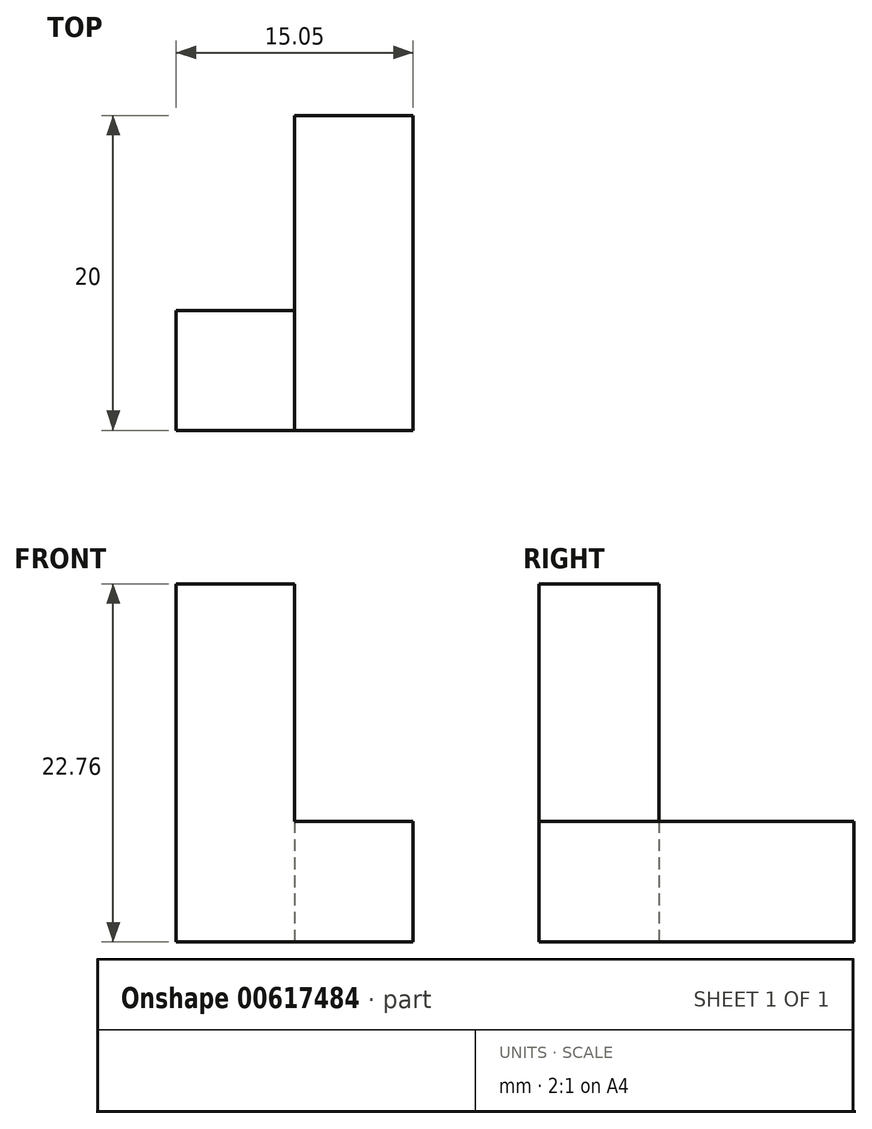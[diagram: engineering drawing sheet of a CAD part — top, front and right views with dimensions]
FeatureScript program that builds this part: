
annotation { "Feature Type Name" : "Feature", "Feature Type Description" : "" }
export const myFeature = defineFeature(function(context is Context, id is Id, definition is map)
    precondition{}
    {
        {
            var Q0;
            Q0=qCreatedBy(makeId("Front.planeOp"),FACE);
            var sketch = newSketch(context, id + "F0", { "sketchPlane" : qUnion([Q0])});
            skLineSegment(sketch, "E0", {"start": v(0, 0) * mm, "end": v(-15.05, 0) * mm});
            skLineSegment(sketch, "E1", {"start": v(-15.05, 0) * mm, "end": v(-15.05, 22.76) * mm});
            skLineSegment(sketch, "E2", {"start": v(-15.05, 22.76) * mm, "end": v(-7.55, 22.76) * mm});
            skLineSegment(sketch, "E3", {"start": v(-7.55, 22.76) * mm, "end": v(-7.55, 7.6) * mm});
            skLineSegment(sketch, "E4", {"start": v(-7.55, 7.6) * mm, "end": v(0, 7.6) * mm});
            skLineSegment(sketch, "E5", {"start": v(0, 7.6) * mm, "end": v(0, 0) * mm});
            skSolve(sketch);
        }
        {
            var Q0;
            Q0 = qSketchRegion(id + "F0", true);
            extrude(context, id + "F1", {"entities" : qUnion([Q0]), "oppositeDirection" : true, "depth" : 7.6 * mm, "offsetDistance" : 25.4 * mm});
        }
        {
            var Q0;
            Q0=qCreatedBy(makeId("Front.planeOp"),FACE);
            var sketch = newSketch(context, id + "F2", { "sketchPlane" : qUnion([Q0])});
            skLineSegment(sketch, "E6", {"start": v(0, 0) * mm, "end": v(0, 7.68) * mm});
            skLineSegment(sketch, "E7", {"start": v(0, 7.68) * mm, "end": v(-7.55, 7.68) * mm});
            skLineSegment(sketch, "E8", {"start": v(-7.55, 7.68) * mm, "end": v(-7.55, 0) * mm});
            skLineSegment(sketch, "E9", {"start": v(-7.55, 0) * mm, "end": v(0, 0) * mm});
            skSolve(sketch);
        }
        {
            var Q0;
            Q0 = qSketchRegion(id + "F2", true);
            extrude(context, id + "F3", {"entities" : qUnion([Q0]), "operationType" : NewBodyOperationType.ADD, "oppositeDirection" : true, "depth" : 20 * mm, "offsetDistance" : 25.4 * mm});
        }
    });
